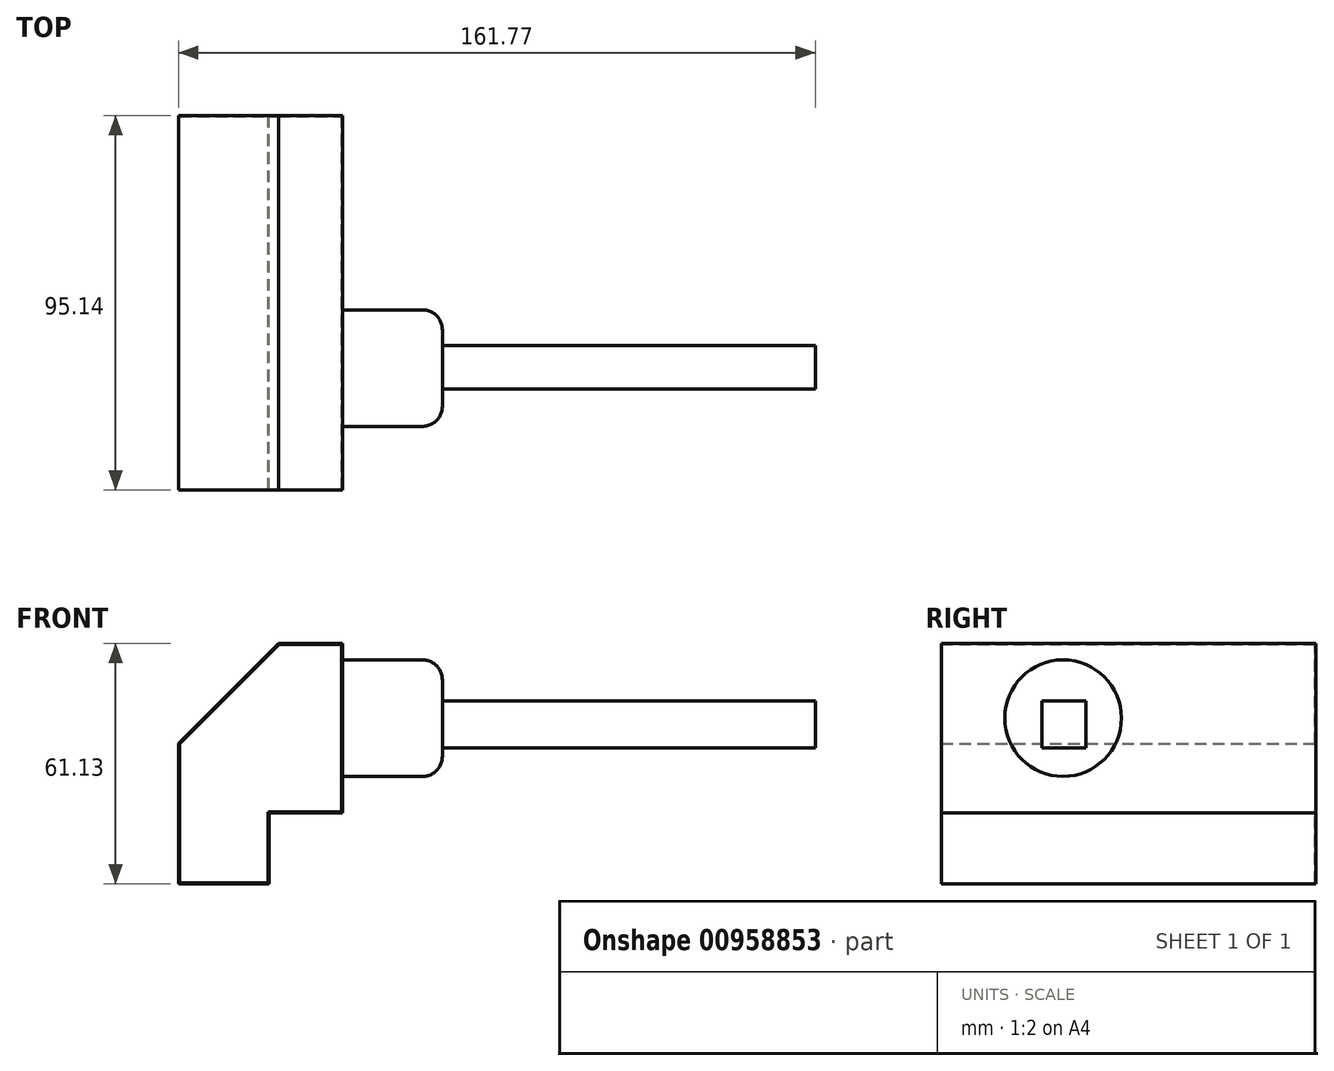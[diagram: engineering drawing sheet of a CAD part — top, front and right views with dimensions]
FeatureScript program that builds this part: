
annotation { "Feature Type Name" : "Feature", "Feature Type Description" : "" }
export const myFeature = defineFeature(function(context is Context, id is Id, definition is map)
    precondition{}
    {
        {
            var Q0;
            Q0=qCreatedBy(makeId("Front.planeOp"),FACE);
            var sketch = newSketch(context, id + "F0", { "sketchPlane" : qUnion([Q0])});
            skLineSegment(sketch, "E0.bottom", {"start": v(32.29, 8.25) * mm, "end": v(13.67, 8.25) * mm});
            skLineSegment(sketch, "E0.top", {"start": v(32.29, 26.3) * mm, "end": v(13.67, 26.3) * mm});
            skLineSegment(sketch, "E0.left", {"start": v(32.29, 8.25) * mm, "end": v(32.29, 26.3) * mm});
            skLineSegment(sketch, "E0.right", {"start": v(13.67, 8.25) * mm, "end": v(13.67, 26.3) * mm});
            skLineSegment(sketch, "E1.bottom", {"start": v(-9.34, 69.38) * mm, "end": v(32.29, 69.38) * mm});
            skLineSegment(sketch, "E1.top", {"start": v(-9.34, 8.25) * mm, "end": v(32.29, 8.25) * mm});
            skLineSegment(sketch, "E1.left", {"start": v(-9.34, 69.38) * mm, "end": v(-9.34, 8.25) * mm});
            skLineSegment(sketch, "E1.right", {"start": v(32.29, 69.38) * mm, "end": v(32.29, 8.25) * mm});
            skLineSegment(sketch, "E2.bottom", {"start": v(56.97, -7.37) * mm, "end": v(38.26, -7.37) * mm});
            skLineSegment(sketch, "E2.top", {"start": v(56.97, -3.16) * mm, "end": v(38.26, -3.16) * mm});
            skLineSegment(sketch, "E2.left", {"start": v(56.97, -7.37) * mm, "end": v(56.97, -3.16) * mm});
            skLineSegment(sketch, "E2.right", {"start": v(38.26, -7.37) * mm, "end": v(38.26, -3.16) * mm});
            skLineSegment(sketch, "E3.bottom", {"start": v(16.82, -19.03) * mm, "end": v(-35.8, -19.03) * mm});
            skLineSegment(sketch, "E3.top", {"start": v(16.82, -11.7) * mm, "end": v(-35.8, -11.7) * mm});
            skLineSegment(sketch, "E3.left", {"start": v(16.82, -19.03) * mm, "end": v(16.82, -11.7) * mm});
            skLineSegment(sketch, "E3.right", {"start": v(-35.8, -19.03) * mm, "end": v(-35.8, -11.7) * mm});
            skSolve(sketch);
        }
        {
            var Q0;
            {var subQ4=sQuery(id+"F0.wireOp",EDGE,"E0.top");Q0=makeQuery(id+"F0.imprint","IMPRINT",FACE,{"disambiguationData":[TD([[makeQuery(id+"F0.imprint","IMPRINT",EDGE,{"derivedFrom":subQ4}),-1.0]])]});}
            extrude(context, id + "F1", {"entities" : qUnion([Q0]), "depth" : 95.14 * mm, "offsetDistance" : 25.4 * mm});
        }
        {
            var Q0;
            Q0=makeQuery(id+"F1.opExtrude","CAP_FACE",FACE,{"disambiguationData":[OSD([sQuery(id+"F0.wireOp",EDGE,"E0.top"),sQuery(id+"F0.wireOp",EDGE,"E0.right"),sQuery(id+"F0.wireOp",EDGE,"E1.bottom"),sQuery(id+"F0.wireOp",EDGE,"E1.top"),sQuery(id+"F0.wireOp",EDGE,"E1.left"),sQuery(id+"F0.wireOp",EDGE,"E1.right")])],"isStart":false});
            var sketch = newSketch(context, id + "F2", { "sketchPlane" : qUnion([Q0])});
            skLineSegment(sketch, "E4.0", {"start": v(-9.34, 32.87) * mm, "end": v(32.29, 32.87) * mm});
            skSolve(sketch);
        }
        {
            var Q0;
            Q0=sQuery(id+"F0.wireOp",EDGE,"E3.bottom");
            extrude(context, id + "F3", {"bodyType" : ToolBodyType.SURFACE, "surfaceEntities" : qUnion([Q0]), "depth" : 25.4 * mm, "offsetDistance" : 25.4 * mm});
        }
        {
            var Q0;
            Q0=makeQuery(id+"F1.opExtrude","SWEPT_EDGE",EDGE,{"disambiguationData":[OSD([sQuery(id+"F0.wireOp",EDGE,"E1.bottom"),sQuery(id+"F0.wireOp",EDGE,"E1.left")])]});
            chamfer(context, id + "F4", {"entities" : qUnion([Q0]), "width" : 25.4 * mm, "tangentPropagation" : true});
        }
        {
            var Q0;
            Q0=makeQuery(id+"F1.opExtrude","CAP_FACE",FACE,{"disambiguationData":[OSD([sQuery(id+"F0.wireOp",EDGE,"E0.top"),sQuery(id+"F0.wireOp",EDGE,"E0.right"),sQuery(id+"F0.wireOp",EDGE,"E1.bottom"),sQuery(id+"F0.wireOp",EDGE,"E1.top"),sQuery(id+"F0.wireOp",EDGE,"E1.left"),sQuery(id+"F0.wireOp",EDGE,"E1.right")])],"isStart":false});
            shell(context, id + "F5", {"entities" : qUnion([Q0]), "thickness" : 0.25 * mm});
        }
        {
            var Q0;
            Q0=makeQuery(id+"F1.opExtrude","SWEPT_FACE",FACE,{"disambiguationData":[OSD([sQuery(id+"F0.wireOp",EDGE,"E1.right")])]});
            var sketch = newSketch(context, id + "F6", { "sketchPlane" : qUnion([Q0])});
            skSolve(sketch);
        }
        {
            var Q0;
            {var subQ0=sQuery(id+"F0.wireOp",EDGE,"E1.right");Q0=makeQuery(id+"F6.imprint","IMPRINT",FACE,{"disambiguationData":[TD([[makeQuery(id+"F6.imprint","IMPRINT",EDGE,{"derivedFrom":makeQuery(id+"F1.opExtrude","CAP_EDGE",EDGE,{"disambiguationData":[OSD([subQ0])],"isStart":true})}),-1.0]])]});}
            var sketch = newSketch(context, id + "F7", { "sketchPlane" : qUnion([Q0])});
            skCircle(sketch, "E5", {"center": v(-64.18, 50.4) * mm, "radius": 14.81 * mm});
            skSolve(sketch);
        }
        {
            var Q0;
            Q0 = qSketchRegion(id + "F7", true);
            var Q1;
            Q1=sQuery(id+"F7.wireOp",EDGE,"E5");
            extrude(context, id + "F8", {"entities" : qUnion([Q0]), "operationType" : NewBodyOperationType.ADD, "surfaceEntities" : qUnion([Q1]), "depth" : 25.4 * mm, "offsetDistance" : 25.4 * mm});
        }
        {
            var Q0;
            Q0=makeQuery(id+"F8.opExtrude","CAP_FACE",FACE,{"disambiguationData":[OSD([sQuery(id+"F7.wireOp",EDGE,"E5")])],"isStart":false});
            var sketch = newSketch(context, id + "F9", { "sketchPlane" : qUnion([Q0])});
            skLineSegment(sketch, "E6.bottom", {"start": v(-69.5, 54.78) * mm, "end": v(-58.42, 54.78) * mm});
            skLineSegment(sketch, "E6.top", {"start": v(-69.5, 42.79) * mm, "end": v(-58.42, 42.79) * mm});
            skLineSegment(sketch, "E6.left", {"start": v(-69.5, 54.78) * mm, "end": v(-69.5, 42.79) * mm});
            skLineSegment(sketch, "E6.right", {"start": v(-58.42, 54.78) * mm, "end": v(-58.42, 42.79) * mm});
            skSolve(sketch);
        }
        {
            var Q0;
            Q0 = qSketchRegion(id + "F9", true);
            extrude(context, id + "F10", {"entities" : qUnion([Q0]), "operationType" : NewBodyOperationType.ADD, "depth" : 94.74 * mm, "offsetDistance" : 25.4 * mm});
        }
        {
            var Q0;
            Q0=makeQuery(id+"F8.opExtrude","CAP_EDGE",EDGE,{"disambiguationData":[OSD([sQuery(id+"F7.wireOp",EDGE,"E5")])],"isStart":false});
            fillet(context, id + "F11", {"entities" : qUnion([Q0]), "radius" : 5.08 * mm, "tangentPropagation" : true, "allowEdgeOverflow" : false});
        }
        {
            var Q0;
            Q0=makeQuery(id+"F1.opExtrude","SWEPT_FACE",FACE,{"disambiguationData":[OSD([sQuery(id+"F0.wireOp",EDGE,"E1.bottom")])]});
            cPlane(context, id + "F12", {"entities" : qUnion([Q0]), "cplaneType" : CPlaneType.OFFSET, "offset" : 41.15 * mm, "width" : 152.4 * mm, "height" : 152.4 * mm});
        }
        {
            var Q0;
            Q0=qCreatedBy(makeId("Front.planeOp"),FACE);
            cPlane(context, id + "F13", {"entities" : qUnion([Q0]), "cplaneType" : CPlaneType.OFFSET, "offset" : 126.24 * mm, "width" : 152.4 * mm, "height" : 152.4 * mm});
        }
        {
            var Q0;
            Q0=makeQuery(id+"F4.opChamfer","BLEND_FACE",FACE,{"disambiguationData":[OSD([sQuery(id+"F0.wireOp",EDGE,"E1.bottom"),sQuery(id+"F0.wireOp",EDGE,"E1.left")])]});
            cPlane(context, id + "F14", {"entities" : qUnion([Q0]), "cplaneType" : CPlaneType.OFFSET, "offset" : 165.6 * mm, "width" : 152.4 * mm, "height" : 152.4 * mm});
        }
    });
